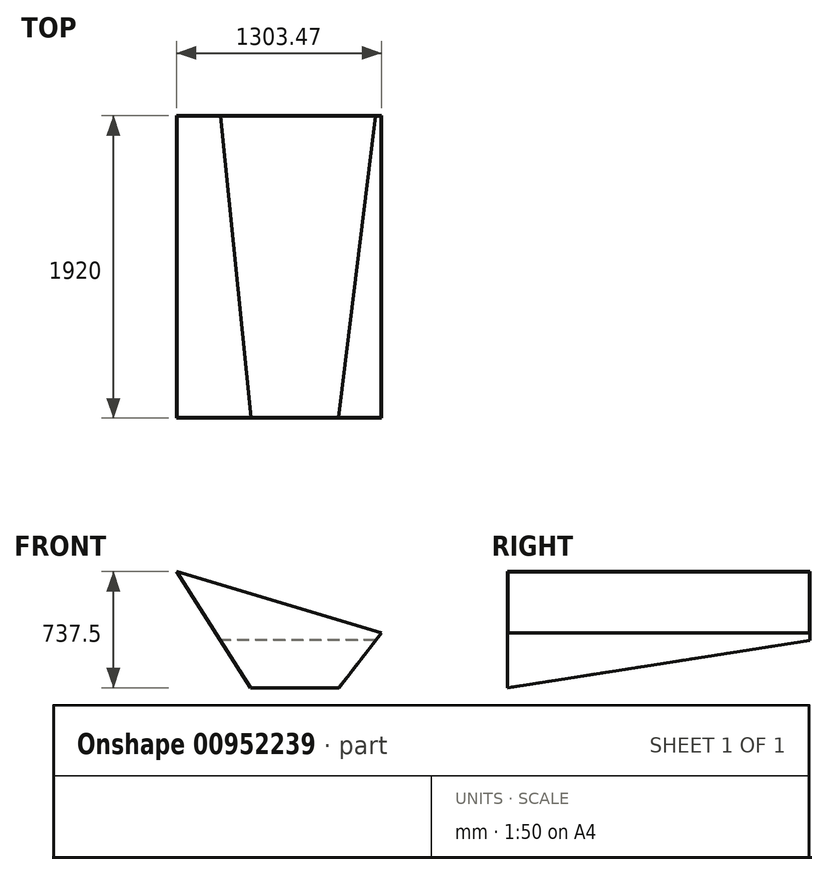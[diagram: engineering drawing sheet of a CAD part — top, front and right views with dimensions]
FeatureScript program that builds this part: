
annotation { "Feature Type Name" : "Feature", "Feature Type Description" : "" }
export const myFeature = defineFeature(function(context is Context, id is Id, definition is map)
    precondition{}
    {
        {
            var Q0;
            Q0=qCreatedBy(makeId("Front.planeOp"),FACE);
            var sketch = newSketch(context, id + "F0", { "sketchPlane" : qUnion([Q0])});
            skLineSegment(sketch, "E0", {"start": v(0, 0) * mm, "end": v(560, 0) * mm});
            skLineSegment(sketch, "E1", {"start": v(560, 0) * mm, "end": v(831.2, 346.48) * mm});
            skLineSegment(sketch, "E2", {"start": v(831.2, 346.48) * mm, "end": v(-472.27, 737.5) * mm});
            skLineSegment(sketch, "E3", {"start": v(-472.27, 737.5) * mm, "end": v(0, 0) * mm});
            skSolve(sketch);
        }
        {
            var Q0;
            Q0=makeQuery(id+"F0.imprint","IMPRINT",FACE,{"disambiguationData":[TD([[makeQuery(id+"F0.imprint","IMPRINT",EDGE,{"derivedFrom":sQuery(id+"F0.wireOp",EDGE,"E0")}),1.0]])]});
            extrude(context, id + "F1", {"entities" : qUnion([Q0]), "oppositeDirection" : true, "depth" : 1920 * mm, "offsetDistance" : 25 * mm});
        }
        {
            var Q0;
            Q0=qCreatedBy(makeId("Right.planeOp"),FACE);
            var sketch = newSketch(context, id + "F2", { "sketchPlane" : qUnion([Q0])});
            skLineSegment(sketch, "E4", {"start": v(1920, 0) * mm, "end": v(1920, 330) * mm});
            skLineSegment(sketch, "E5.MirrorCS", {"start": v(1920, 300) * mm, "end": v(0, 0) * mm});
            skLineSegment(sketch, "E6.MirrorCS", {"start": v(0, 0) * mm, "end": v(1920, 0) * mm});
            skLineSegment(sketch, "E7", {"start": v(1920, 300) * mm, "end": v(1920, 0) * mm});
            skSolve(sketch);
        }
        {
            var Q0;
            Q0 = qSketchRegion(id + "F2", true);
            extrude(context, id + "F3", {"entities" : qUnion([Q0]), "operationType" : NewBodyOperationType.REMOVE, "endBound" : BoundingType.THROUGH_ALL, "depth" : 25 * mm, "offsetDistance" : 25 * mm, "hasSecondDirection" : true, "secondDirectionBound" : SecondDirectionBoundingType.THROUGH_ALL, "secondDirectionOppositeDirection" : true, "secondDirectionDepth" : 25 * mm});
        }
        {
            var Q0;
            Q0=makeQuery(id+"F1.opExtrude","SWEPT_FACE",FACE,{"disambiguationData":[OSD([sQuery(id+"F0.wireOp",EDGE,"E2")])]});
            shell(context, id + "F4", {"entities" : qUnion([Q0]), "thickness" : 3 * mm});
        }
    });
